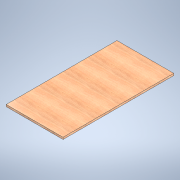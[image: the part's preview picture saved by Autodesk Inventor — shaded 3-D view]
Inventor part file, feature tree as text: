
AUTODESK INVENTOR PART (.ipt)
format: ipt  version: 2022 (Build 260153000, 153)  size: 107,008 bytes
history: native  units: mm
features: extrude x1, sketch x1
ambient origin geometry x8: Origin, YZ Plane, XZ Plane, XY Plane, X Axis, Y Axis, Z Axis, Center Point
bodies: Solid1 (feature_tree)
feature tree (2):
  extrude  "Extrusion1"  Depth=590.0mm
  sketch  "Sketch1"  dims[d0=1150.0mm d1=590.0mm d2=20.0mm d3=0.0mm]
